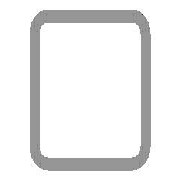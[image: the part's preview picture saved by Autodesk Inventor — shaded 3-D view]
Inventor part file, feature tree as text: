
AUTODESK INVENTOR PART (.ipt)
format: ipt  version: 2018 (Build 220112000, 112)  size: 144,384 bytes
history: native  units: mm (DEFAULTED — no unit token found)
features: sketch x4, other x3, extrude x1, hole x1, plane x1
ambient origin geometry x8: Origin, YZ Plane, XZ Plane, XY Plane, X Axis, Y Axis, Z Axis, Center Point
bodies: Solid1 (feature_tree)
feature tree (10):
  other  "Driven Length"
  other  "Piano iniziale"
  other  "Piano finale"
  extrude  "Corpo"  TaperAngle=0.0deg  [1 undecoded]
  hole  "Foro1"  [1 undecoded]
  sketch  "Schizzo"
  sketch  "Sketch3"  dims[d3=620.0mm d4=0.0mm]
  plane  "Work Plane3"
  sketch  "Sketch4"  dims[d7=4.0mm d9=40.0mm d11=40.0mm d12=2.0mm d13=-0.0mm d14=620.0mm d15=20.0mm d16=20.0mm d17=90.0deg d18=620.0mm d22=105.0mm d23=10.0mm d24=6.0mm d25=4.0mm d26=2.0mm d27=90.0deg d28=5.0mm d29=20.594885mm d30=12.5mm d31=75.0mm d32=105.0mm d33=105.0mm]
  sketch  "Schizzo5"
note: 2 required parameter values undecoded (feature->parameter linkage not recoverable at this tier; creation-order binding heuristic only, values carry confidence <= 0.55)
